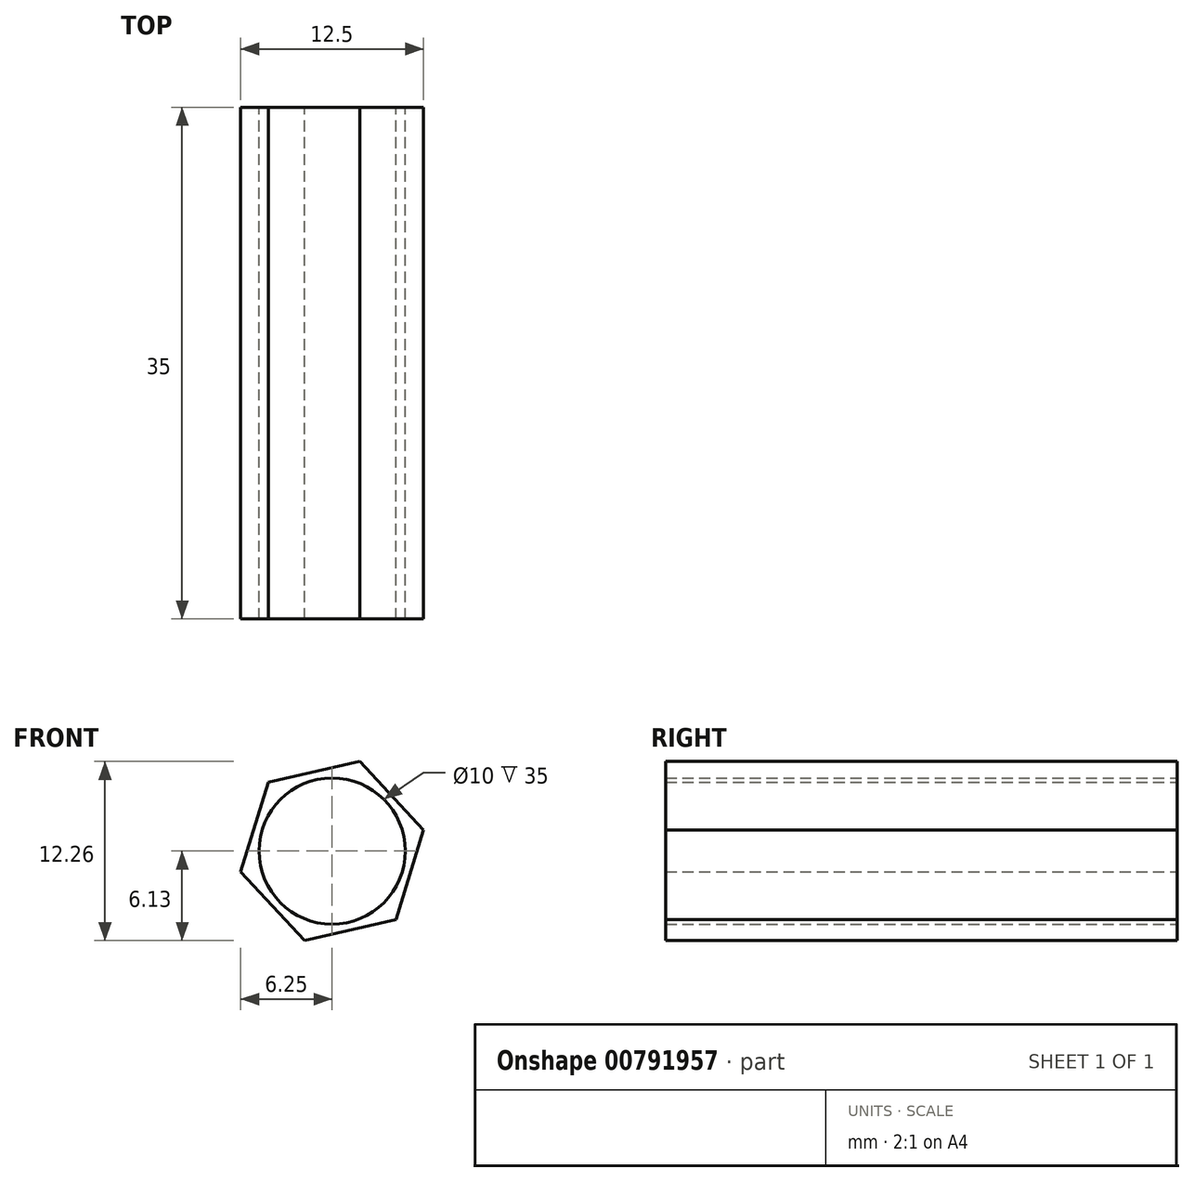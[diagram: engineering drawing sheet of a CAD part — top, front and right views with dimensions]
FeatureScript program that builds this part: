
annotation { "Feature Type Name" : "Feature", "Feature Type Description" : "" }
export const myFeature = defineFeature(function(context is Context, id is Id, definition is map)
    precondition{}
    {
        {
            var Q0;
            Q0=qCreatedBy(makeId("Front.planeOp"),FACE);
            var sketch = newSketch(context, id + "F0", { "sketchPlane" : qUnion([Q0])});
            skCircle(sketch, "E0.cCircle", {"center": v(0, 0) * mm, "radius": 5.55 * mm, "construction": true});
            skLineSegment(sketch, "E0.0", {"start": v(1.9, 6.13) * mm, "end": v(6.25, 1.43) * mm});
            skLineSegment(sketch, "E0.1", {"start": v(6.25, 1.43) * mm, "end": v(4.36, -4.7) * mm});
            skLineSegment(sketch, "E0.2", {"start": v(4.36, -4.7) * mm, "end": v(-1.9, -6.13) * mm});
            skLineSegment(sketch, "E0.3", {"start": v(-1.9, -6.13) * mm, "end": v(-6.25, -1.43) * mm});
            skLineSegment(sketch, "E0.4", {"start": v(-6.25, -1.43) * mm, "end": v(-4.36, 4.7) * mm});
            skLineSegment(sketch, "E0.5", {"start": v(-4.36, 4.7) * mm, "end": v(1.9, 6.13) * mm});
            skPoint(sketch, "E0.0.midPoint", {"position": v(4.07, 3.78) * mm});
            skSolve(sketch);
        }
        {
            var Q0;
            Q0=makeQuery(id+"F0.imprint","IMPRINT",FACE,{"disambiguationData":[TD([[makeQuery(id+"F0.imprint","IMPRINT",EDGE,{"derivedFrom":sQuery(id+"F0.wireOp",EDGE,"E0.0")}),-1.0]])]});
            extrude(context, id + "F1", {"entities" : qUnion([Q0]), "depth" : 35 * mm, "offsetDistance" : 25 * mm});
        }
        {
            var Q0;
            Q0=makeQuery(id+"F1.opExtrude","CAP_FACE",FACE,{"disambiguationData":[OSD([sQuery(id+"F0.wireOp",EDGE,"E0.0"),sQuery(id+"F0.wireOp",EDGE,"E0.1"),sQuery(id+"F0.wireOp",EDGE,"E0.2"),sQuery(id+"F0.wireOp",EDGE,"E0.3"),sQuery(id+"F0.wireOp",EDGE,"E0.4"),sQuery(id+"F0.wireOp",EDGE,"E0.5")])],"isStart":true});
            var sketch = newSketch(context, id + "F2", { "sketchPlane" : qUnion([Q0])});
            skCircle(sketch, "E1", {"center": v(0, 0) * mm, "radius": 5 * mm});
            skSolve(sketch);
        }
        {
            var Q0;
            Q0 = qSketchRegion(id + "F2", true);
            extrude(context, id + "F3", {"entities" : qUnion([Q0]), "operationType" : NewBodyOperationType.REMOVE, "endBound" : BoundingType.THROUGH_ALL, "oppositeDirection" : true, "depth" : 25 * mm, "offsetDistance" : 25 * mm});
        }
    });
